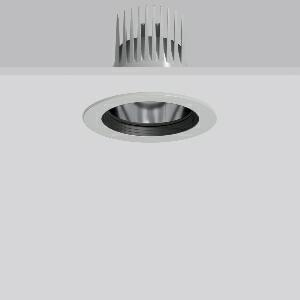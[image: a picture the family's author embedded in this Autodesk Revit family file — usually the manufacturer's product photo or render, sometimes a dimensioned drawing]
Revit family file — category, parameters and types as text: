
# Revit family: heledon_maxi_e_901766_004_2_832c
name_source: partatom
category: Lighting Fixtures
units: mm (PartAtom-declared; Revit-internal decimal feet)

## family parameters
Cut with Voids When Loaded = No
Host = Face
Light Source = No
Part Type = Normal
Room Calculation Point = No
Round Connector Dimension = Use Diameter
Shared = No

## types (1)
- HELEDON maxi E (1 x LED Modul 927, 3950 lm, 2700)
    Apparent Load = 35 VA
    Approval mark = CE
    CIE Flux Codes = 97 100 100 100 100
    Color Rendering = 92
    Color Temperature = 2700
    Default Elevation = 1800 mm
    Description = Series: HELEDON maxi
Round recessed downlight. Housing: die-cast aluminium, powder-coated. Black plastic ring and recessed LED to prevent glare from the side. Optical assembly with reflector made of MIRO-Silver with 98% total light reflection for outstanding efficiency - can be changed without tools. Best colour rendering index Ra>90. Suitable for Recessed ceiling mounting. Installation without tools thanks to spring fastening system. Including separate LED converter with connecting cable 600 mm.High quality converter without flickering and stroboscopic effect. Through-wiring box (5 pole) available as accessory. The following accessories can be mounted without use of tools: interchangeable lenses, decorative glasses, honeycomb louvre, clear and frosted diffusers, white interchangeable plastic ring. 
Colour: silver
Diameter: 162 mm
Height: 3 mm
Cut-out diameter: 152 mm
Recess height: 200 mm
Luminaire: recess height: 135 mm
Lamp: LED
Socket: without socket
Colour temperature: 2700K
Colour rendering index (CRI): 92
System power: 35 W
Rated luminous flux: 3950 lm
Luminous efficiency: 113 lm/W
Control gear: Regulated power supply
Protection class: II
Type of protection: IP 20
    Height = 0 mm  [stored 0 ft]
    Lamp = 1 x LED Modul 927
    Lamp Light Flux = 3950 lm
    Lamp count = 1
    Length = 162 mm
    Lifetime = 50000 h
    Luminous efficacy = 113 lm/W
    Manufacturer = RZB
    ModVariant = No
    Model = 901766.004.2
    Mounting Place = Ceiling
    Mounting Type = Recessed
    Number of Poles = 1
    OnlyDefault = Yes
    Power Factor = 1
    Product Name = HELEDON maxi E
    Product group = Recessed downlights
    ProductGroupID = 402
    Protection Class = Protection class II
    Protection Degree = IP 20
    RLX_Detail_Level = 1
    RLX_Emergency_Light_Flux = 0 lm
    RLX_Emergency_Type = 0
    RLX_Emergency_Type_DB = No
    RlxData = <blob elided: 118997 chars, md5=0e9e6040>
    Socket = socket
    Standby Power = 0 W
    System Light Flux = 3950 lm
    System Power = 35 W
    Type Comments = Product without accessories
    Type Image = 901662.004.jpg
    URL = http://relux.com
    VarID = ---
    Voltage = 230 V
    Voltage Range = 220-240 V
    Weight = 0.00 kg
    Width = 0 mm  [stored 0 ft]

note: [stored X ft] marks values corroborated as IEEE doubles in the binary element streams (Revit-internal decimal feet)

## geometry (parser evidence)
native form markers: Blend x4, Sweep x10
no freeform markers — native parametric forms only
